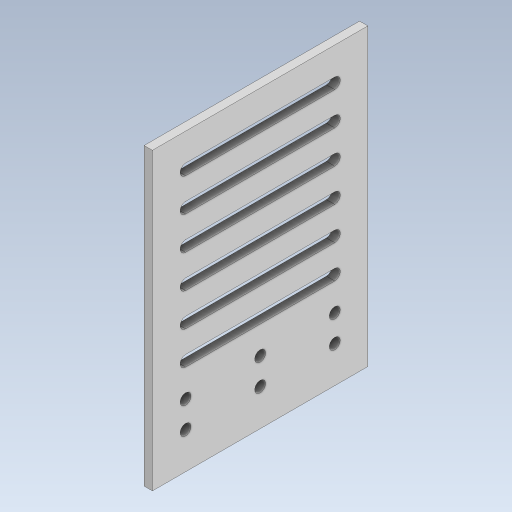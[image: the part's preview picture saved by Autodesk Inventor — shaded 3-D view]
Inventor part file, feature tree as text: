
AUTODESK INVENTOR PART (.ipt)
format: ipt  version: 2023.5 (Build 275446000, 446)  size: 167,936 bytes
history: native  units: mm
features: extrude x1, sketch x1
ambient origin geometry x8: Origin, YZ Plane, XZ Plane, XY Plane, X Axis, Y Axis, Z Axis, Center Point
bodies: Body1 (feature_tree)
feature tree (2):
  extrude  "Extrusion2"  Depth=3.3mm
  sketch  "Sketch1"  dims[d0=3.3mm d1=3.3mm d5=3.3mm d22=10.0mm d23=10.0mm d24=22.5mm d25=22.5mm d26=3.3mm d27=3.3mm d28=2.5mm d29=0.0mm d30=70.0mm d31=3.3mm d32=10.0mm d33=3.3mm d34=60.0mm d36=10.0mm d37=10.0mm d39=10.0mm]
